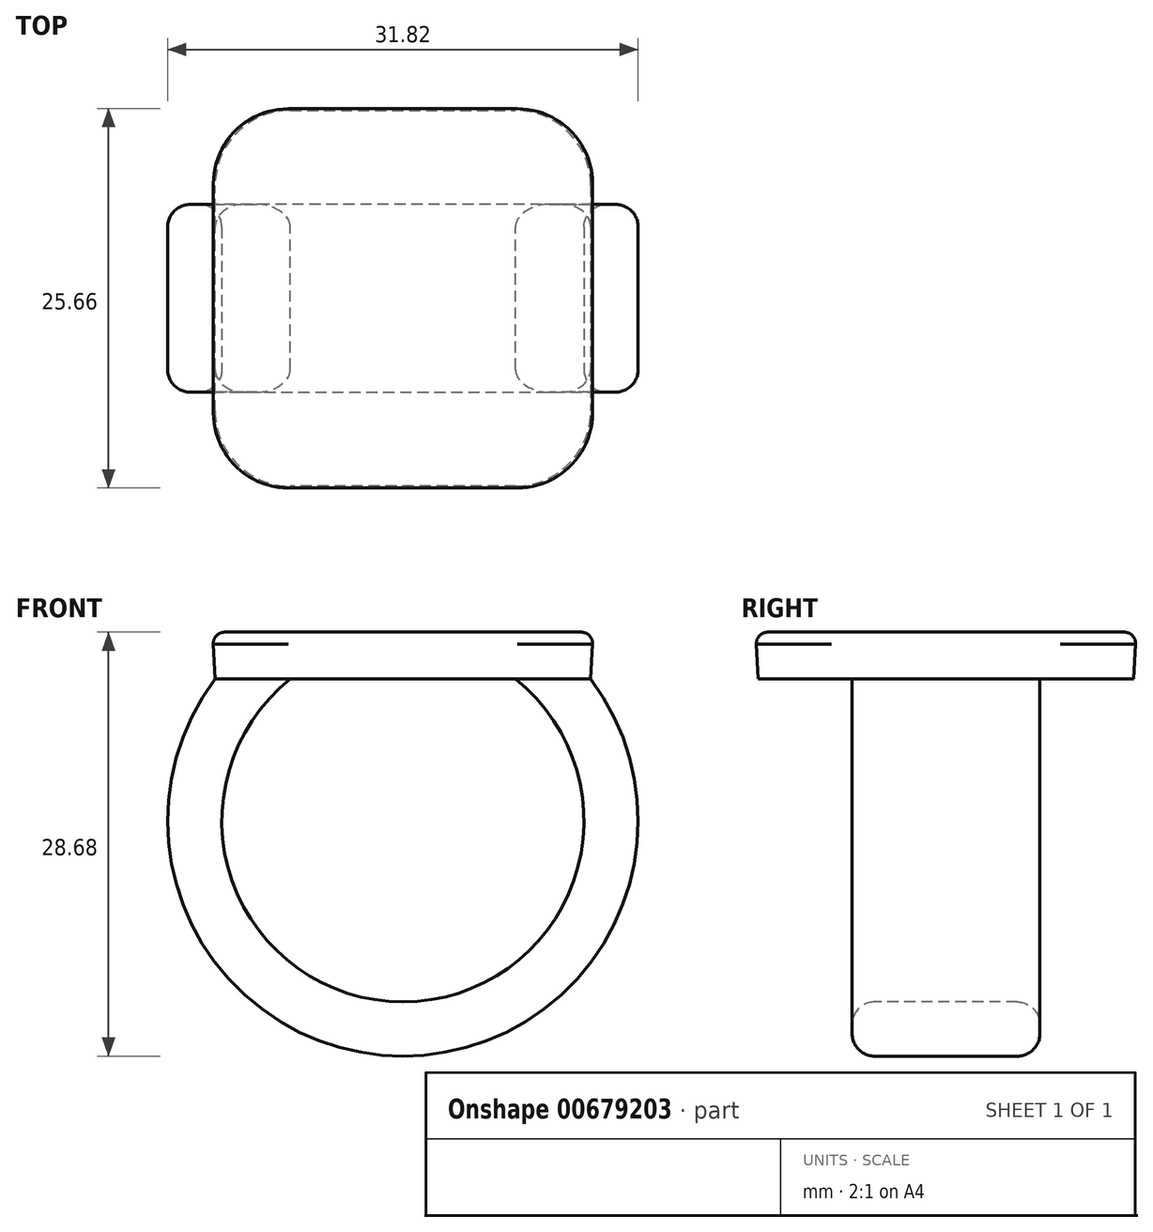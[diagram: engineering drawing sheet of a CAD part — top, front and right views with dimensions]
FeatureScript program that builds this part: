
annotation { "Feature Type Name" : "Feature", "Feature Type Description" : "" }
export const myFeature = defineFeature(function(context is Context, id is Id, definition is map)
    precondition{}
    {
        {
            var Q0;
            Q0=qCreatedBy(makeId("Top.planeOp"),FACE);
            var sketch = newSketch(context, id + "F0", { "sketchPlane" : qUnion([Q0])});
            skLineSegment(sketch, "E0.bottom", {"start": v(12.7, 12.7) * mm, "end": v(-12.7, 12.7) * mm});
            skLineSegment(sketch, "E0.top", {"start": v(12.7, -12.7) * mm, "end": v(-12.7, -12.7) * mm});
            skLineSegment(sketch, "E0.left", {"start": v(12.7, 12.7) * mm, "end": v(12.7, -12.7) * mm});
            skLineSegment(sketch, "E0.right", {"start": v(-12.7, 12.7) * mm, "end": v(-12.7, -12.7) * mm});
            skPoint(sketch, "E0.middle", {"position": v(0, 0) * mm});
            skSolve(sketch);
        }
        {
            var Q0;
            Q0 = qSketchRegion(id + "F0", true);
            extrude(context, id + "F1", {"entities" : qUnion([Q0]), "depth" : 3.17 * mm, "offsetDistance" : 25 * mm, "hasDraft" : true, "draftAngle" : 3 * degree});
        }
        {
            var Q0;
            Q0=qCreatedBy(makeId("Front.planeOp"),FACE);
            var sketch = newSketch(context, id + "F2", { "sketchPlane" : qUnion([Q0])});
            skArc(sketch, "E1", {"start": v(-10.16, 0) * mm, "mid": v(0, -23.56) * mm, "end": v(10.16, 0) * mm});
            skSolve(sketch);
        }
        {
            var Q0;
            Q0=qCreatedBy(makeId("Top.planeOp"),FACE);
            var sketch = newSketch(context, id + "F3", { "sketchPlane" : qUnion([Q0])});
            skLineSegment(sketch, "E2.bottom", {"start": v(-12.7, -6.35) * mm, "end": v(-7.62, -6.35) * mm});
            skLineSegment(sketch, "E2.top", {"start": v(-12.7, 6.35) * mm, "end": v(-7.62, 6.35) * mm});
            skLineSegment(sketch, "E2.left", {"start": v(-12.7, -6.35) * mm, "end": v(-12.7, 6.35) * mm});
            skLineSegment(sketch, "E2.right", {"start": v(-7.62, -6.35) * mm, "end": v(-7.62, 6.35) * mm});
            skPoint(sketch, "E2.middle", {"position": v(-10.16, 0) * mm});
            skSolve(sketch);
        }
        {
            var Q0;
            Q0=makeQuery(id+"F3.imprint","IMPRINT",FACE,{"disambiguationData":[TD([[makeQuery(id+"F3.imprint","IMPRINT",EDGE,{"derivedFrom":sQuery(id+"F3.wireOp",EDGE,"E2.bottom")}),1.0]])]});
            var Q1;
            Q1=sQuery(id+"F2.wireOp",EDGE,"E1");
            sweep(context, id + "F4", {"operationType" : NewBodyOperationType.ADD, "profiles" : qUnion([Q0]), "path" : qUnion([Q1])});
        }
        {
            var Q0;
            Q0=qCreatedBy(makeId("Front.planeOp"),FACE);
            var sketch = newSketch(context, id + "F5", { "sketchPlane" : qUnion([Q0])});
            skArc(sketch, "E3.0", {"start": v(-7.62, 0) * mm, "mid": v(-1.74, -21.71) * mm, "end": v(10.01, -2.54) * mm});
            skArc(sketch, "E4.0", {"start": v(-7.62, 0) * mm, "mid": v(0, -21.84) * mm, "end": v(7.62, 0) * mm});
            skLineSegment(sketch, "E5", {"start": v(7.62, 0) * mm, "end": v(10.16, 0) * mm});
            skLineSegment(sketch, "E6", {"start": v(10.16, 0) * mm, "end": v(10.01, -2.54) * mm});
            skSolve(sketch);
        }
        {
            var Q0;
            {var subQ0=sQuery(id+"F5.wireOp",EDGE,"E5");Q0=makeQuery(id+"F5.imprint","IMPRINT",FACE,{"disambiguationData":[TD([[makeQuery(id+"F5.imprint","IMPRINT",EDGE,{"derivedFrom":subQ0}),-1.0]])]});}
            var Q1;
            Q1=makeQuery(id+"F4.opSweep","SWEPT_FACE",FACE,{"disambiguationData":[OSD([sQuery(id+"F2.wireOp",EDGE,"E1"),sQuery(id+"F3.wireOp",EDGE,"E2.bottom")])]});
            var Q2;
            Q2=makeQuery(id+"F4.opSweep","SWEPT_FACE",FACE,{"disambiguationData":[OSD([sQuery(id+"F2.wireOp",EDGE,"E1"),sQuery(id+"F3.wireOp",EDGE,"E2.top")])]});
            extrude(context, id + "F6", {"entities" : qUnion([Q0]), "operationType" : NewBodyOperationType.ADD, "endBound" : BoundingType.UP_TO_SURFACE, "depth" : 25 * mm, "endBoundEntityFace" : qUnion([Q1]), "offsetDistance" : 25 * mm, "hasSecondDirection" : true, "secondDirectionBound" : SecondDirectionBoundingType.UP_TO_SURFACE, "secondDirectionOppositeDirection" : true, "secondDirectionDepth" : 25 * mm, "secondDirectionBoundEntityFace" : qUnion([Q2])});
        }
        {
            var Q0;
            Q0=makeQuery(id+"F1.opExtrude","SWEPT_EDGE",EDGE,{"disambiguationData":[OSD([sQuery(id+"F0.wireOp",EDGE,"E0.top"),sQuery(id+"F0.wireOp",EDGE,"E0.right")])]});
            var Q1;
            Q1=makeQuery(id+"F1.opExtrude","SWEPT_EDGE",EDGE,{"disambiguationData":[OSD([sQuery(id+"F0.wireOp",EDGE,"E0.top"),sQuery(id+"F0.wireOp",EDGE,"E0.left")])]});
            var Q2;
            Q2=makeQuery(id+"F1.opExtrude","SWEPT_EDGE",EDGE,{"disambiguationData":[OSD([sQuery(id+"F0.wireOp",EDGE,"E0.bottom"),sQuery(id+"F0.wireOp",EDGE,"E0.left")])]});
            var Q3;
            Q3=makeQuery(id+"F1.opExtrude","SWEPT_EDGE",EDGE,{"disambiguationData":[OSD([sQuery(id+"F0.wireOp",EDGE,"E0.bottom"),sQuery(id+"F0.wireOp",EDGE,"E0.right")])]});
            fillet(context, id + "F7", {"entities" : qUnion([Q0, Q1, Q2, Q3]), "radius" : 5.08 * mm, "tangentPropagation" : true, "allowEdgeOverflow" : false});
        }
        {
            var Q0;
            Q0=makeQuery(id+"F4.opSweep","SWEPT_EDGE",EDGE,{"disambiguationData":[OSD([sQuery(id+"F2.wireOp",EDGE,"E1"),sQuery(id+"F3.wireOp",EDGE,"E2.bottom"),sQuery(id+"F3.wireOp",EDGE,"E2.left")])]});
            var Q1;
            {var subQ0=sQuery(id+"F5.wireOp",EDGE,"E4.0");var subQ1=sQuery(id+"F3.wireOp",EDGE,"E2.bottom");var subQ2=sQuery(id+"F2.wireOp",EDGE,"E1");Q1=makeQuery(id+"F6.boolean.opBoolean","MERGE",EDGE,{"derivedFrom":[makeQuery(id+"F4.opSweep","SWEPT_EDGE",EDGE,{"disambiguationData":[OSD([subQ2,subQ1,sQuery(id+"F3.wireOp",EDGE,"E2.right")])]}),makeQuery(id+"F6.opExtrude","TWEAK_EDGE",EDGE,{"derivedFrom":[makeQuery(id+"F4.opSweep","SWEPT_FACE",FACE,{"disambiguationData":[OSD([subQ2,subQ1])]}),makeQuery(id+"F5.imprint","IMPRINT",EDGE,{"disambiguationData":[TD([[makeQuery(id+"F5.imprint","INTERSECT",VERTEX,{"derivedFrom":[subQ0,sQuery(id+"F5.wireOp",EDGE,"E5")]}),1.0]])],"derivedFrom":subQ0})]})]});}
            var Q2;
            Q2=makeQuery(id+"F4.opSweep","SWEPT_EDGE",EDGE,{"disambiguationData":[OSD([sQuery(id+"F2.wireOp",EDGE,"E1"),sQuery(id+"F3.wireOp",EDGE,"E2.top"),sQuery(id+"F3.wireOp",EDGE,"E2.left")])]});
            var Q3;
            {var subQ0=sQuery(id+"F5.wireOp",EDGE,"E4.0");var subQ1=sQuery(id+"F3.wireOp",EDGE,"E2.top");var subQ2=sQuery(id+"F2.wireOp",EDGE,"E1");Q3=makeQuery(id+"F6.boolean.opBoolean","MERGE",EDGE,{"derivedFrom":[makeQuery(id+"F4.opSweep","SWEPT_EDGE",EDGE,{"disambiguationData":[OSD([subQ2,subQ1,sQuery(id+"F3.wireOp",EDGE,"E2.right")])]}),makeQuery(id+"F6.opExtrude","TWEAK_EDGE",EDGE,{"derivedFrom":[makeQuery(id+"F4.opSweep","SWEPT_FACE",FACE,{"disambiguationData":[OSD([subQ2,subQ1])]}),makeQuery(id+"F5.imprint","IMPRINT",EDGE,{"disambiguationData":[TD([[makeQuery(id+"F5.imprint","INTERSECT",VERTEX,{"derivedFrom":[subQ0,sQuery(id+"F5.wireOp",EDGE,"E5")]}),1.0]])],"derivedFrom":subQ0})]})]});}
            fillet(context, id + "F8", {"entities" : qUnion([Q0, Q1, Q2, Q3]), "radius" : 1.52 * mm, "tangentPropagation" : true, "allowEdgeOverflow" : false});
        }
        {
            var Q0;
            Q0=makeQuery(id+"F1.opExtrude","CAP_EDGE",EDGE,{"disambiguationData":[OSD([sQuery(id+"F0.wireOp",EDGE,"E0.top")])],"isStart":false});
            var Q1;
            Q1=makeQuery(id+"F1.opExtrude","CAP_EDGE",EDGE,{"disambiguationData":[OSD([sQuery(id+"F0.wireOp",EDGE,"E0.right")])],"isStart":false});
            var Q2;
            Q2=makeQuery(id+"F1.opExtrude","CAP_EDGE",EDGE,{"disambiguationData":[OSD([sQuery(id+"F0.wireOp",EDGE,"E0.bottom")])],"isStart":false});
            var Q3;
            Q3=makeQuery(id+"F1.opExtrude","CAP_FACE",FACE,{"disambiguationData":[OSD([sQuery(id+"F0.wireOp",EDGE,"E0.bottom"),sQuery(id+"F0.wireOp",EDGE,"E0.top"),sQuery(id+"F0.wireOp",EDGE,"E0.left"),sQuery(id+"F0.wireOp",EDGE,"E0.right")])],"isStart":false});
            var Q4;
            {var subQ0=sQuery(id+"F0.wireOp",EDGE,"E0.left");var subQ1=sQuery(id+"F0.wireOp",EDGE,"E0.top");Q4=makeQuery(id+"F7.opFillet","BLEND_EDGE",EDGE,{"blendedFrom":[makeQuery(id+"F1.opExtrude","SWEPT_EDGE",EDGE,{"disambiguationData":[OSD([subQ1,subQ0])]}),makeQuery(id+"F1.opExtrude","CAP_FACE",FACE,{"disambiguationData":[OSD([sQuery(id+"F0.wireOp",EDGE,"E0.bottom"),subQ1,subQ0,sQuery(id+"F0.wireOp",EDGE,"E0.right")])],"isStart":false})],"blendedInto":[makeQuery(id+"F1.opExtrude","CAP_FACE",FACE,{"disambiguationData":[OSD([sQuery(id+"F0.wireOp",EDGE,"E0.bottom"),subQ1,subQ0,sQuery(id+"F0.wireOp",EDGE,"E0.right")])],"isStart":false})]});}
            var Q5;
            Q5=makeQuery(id+"F1.opExtrude","CAP_EDGE",EDGE,{"disambiguationData":[OSD([sQuery(id+"F0.wireOp",EDGE,"E0.left")])],"isStart":false});
            var Q6;
            {var subQ0=sQuery(id+"F0.wireOp",EDGE,"E0.left");var subQ1=sQuery(id+"F0.wireOp",EDGE,"E0.bottom");Q6=makeQuery(id+"F7.opFillet","BLEND_EDGE",EDGE,{"blendedFrom":[makeQuery(id+"F1.opExtrude","SWEPT_EDGE",EDGE,{"disambiguationData":[OSD([subQ1,subQ0])]}),makeQuery(id+"F1.opExtrude","CAP_FACE",FACE,{"disambiguationData":[OSD([subQ1,sQuery(id+"F0.wireOp",EDGE,"E0.top"),subQ0,sQuery(id+"F0.wireOp",EDGE,"E0.right")])],"isStart":false})],"blendedInto":[makeQuery(id+"F1.opExtrude","CAP_FACE",FACE,{"disambiguationData":[OSD([subQ1,sQuery(id+"F0.wireOp",EDGE,"E0.top"),subQ0,sQuery(id+"F0.wireOp",EDGE,"E0.right")])],"isStart":false})]});}
            var Q7;
            {var subQ0=sQuery(id+"F0.wireOp",EDGE,"E0.right");var subQ1=sQuery(id+"F0.wireOp",EDGE,"E0.top");Q7=makeQuery(id+"F7.opFillet","BLEND_EDGE",EDGE,{"blendedFrom":[makeQuery(id+"F1.opExtrude","SWEPT_EDGE",EDGE,{"disambiguationData":[OSD([subQ1,subQ0])]}),makeQuery(id+"F1.opExtrude","CAP_FACE",FACE,{"disambiguationData":[OSD([sQuery(id+"F0.wireOp",EDGE,"E0.bottom"),subQ1,sQuery(id+"F0.wireOp",EDGE,"E0.left"),subQ0])],"isStart":false})],"blendedInto":[makeQuery(id+"F1.opExtrude","CAP_FACE",FACE,{"disambiguationData":[OSD([sQuery(id+"F0.wireOp",EDGE,"E0.bottom"),subQ1,sQuery(id+"F0.wireOp",EDGE,"E0.left"),subQ0])],"isStart":false})]});}
            fillet(context, id + "F9", {"entities" : qUnion([Q0, Q1, Q2, Q3, Q4, Q5, Q6, Q7]), "radius" : 0.76 * mm, "tangentPropagation" : true, "allowEdgeOverflow" : false});
        }
    });
